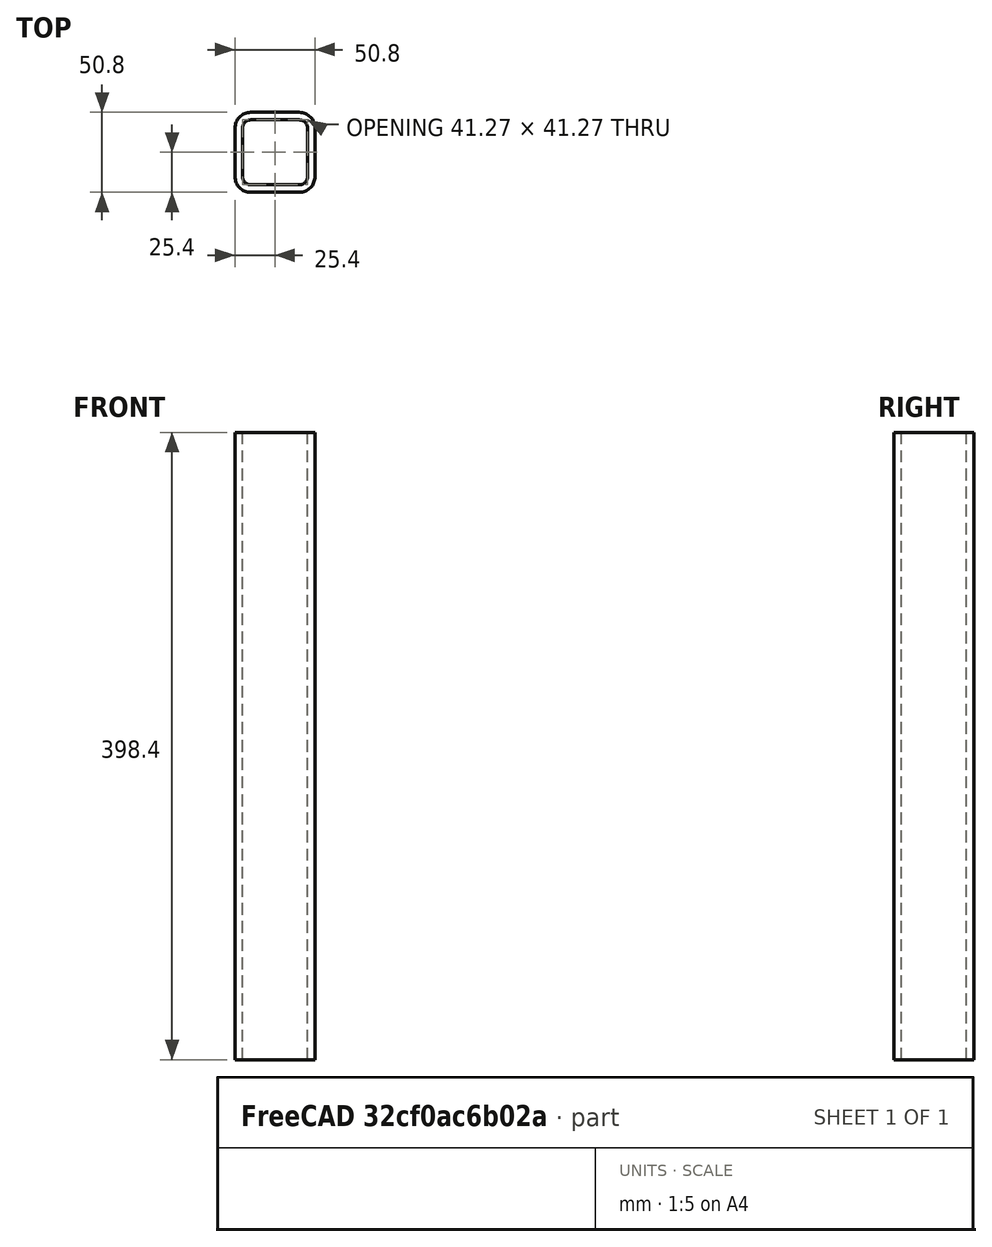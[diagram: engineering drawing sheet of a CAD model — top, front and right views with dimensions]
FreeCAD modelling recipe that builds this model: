
FCSTD DOCUMENT  (FreeCAD 0.19R23578 (Git))
Label: frame_side_piece
License: All rights reserved
LicenseURL: http://en.wikipedia.org/wiki/All_rights_reserved
objects: PartDesign::CoordinateSystem×2, Sketcher::SketchObject×1, PartDesign::Pad×1, PartDesign::Body×1, App::Part×1
note: 6 computed .brp shape members not serialized (recipe doc carries the construction recipe); baked Part::Feature solids carry a one-line shape summary decoded from their .brp

FEATURE [Sketcher::SketchObject] Sketch004
  MapMode = 5
  sketch-geometry (16):
    g0: LineSegment StartX=10 StartY=0 StartZ=0 EndX=40.8 EndY=0 EndZ=0
    g1: LineSegment StartX=50.8 StartY=10 StartZ=0 EndX=50.8 EndY=40.8 EndZ=0
    g2: LineSegment StartX=40.8 StartY=50.8 StartZ=0 EndX=10 EndY=50.8 EndZ=0
    g3: LineSegment StartX=0 StartY=40.8 StartZ=0 EndX=0 EndY=10 EndZ=0
    g4: ArcOfCircle CenterX=10 CenterY=40.8 CenterZ=0 NormalX=0 NormalY=0 NormalZ=1 AngleXU=0 Radius=10 StartAngle=1.5708 EndAngle=3.14159
    g5: ArcOfCircle CenterX=10 CenterY=10 CenterZ=0 NormalX=0 NormalY=0 NormalZ=1 AngleXU=0 Radius=10 StartAngle=3.14159 EndAngle=4.71239
    g6: ArcOfCircle CenterX=40.8 CenterY=10 CenterZ=0 NormalX=0 NormalY=0 NormalZ=1 AngleXU=0 Radius=10 StartAngle=4.71239 EndAngle=6.28319
    g7: ArcOfCircle CenterX=40.8 CenterY=40.8 CenterZ=0 NormalX=0 NormalY=0 NormalZ=1 AngleXU=0 Radius=10 StartAngle=0 EndAngle=1.5708
    g8: LineSegment StartX=10 StartY=46.0375 StartZ=0 EndX=40.8 EndY=46.0375 EndZ=0
    g9: LineSegment StartX=46.0375 StartY=40.8 StartZ=0 EndX=46.0375 EndY=10 EndZ=0
    g10: LineSegment StartX=40.8 StartY=4.7625 StartZ=0 EndX=10 EndY=4.7625 EndZ=0
    g11: LineSegment StartX=4.7625 StartY=10 StartZ=0 EndX=4.7625 EndY=40.8 EndZ=0
    g12: ArcOfCircle CenterX=10 CenterY=40.8 CenterZ=0 NormalX=0 NormalY=0 NormalZ=1 AngleXU=0 Radius=5.2375 StartAngle=1.5708 EndAngle=3.14159
    g13: ArcOfCircle CenterX=10 CenterY=10 CenterZ=0 NormalX=0 NormalY=0 NormalZ=1 AngleXU=0 Radius=5.2375 StartAngle=3.14159 EndAngle=4.71239
    g14: ArcOfCircle CenterX=40.8 CenterY=10 CenterZ=0 NormalX=0 NormalY=0 NormalZ=1 AngleXU=0 Radius=5.2375 StartAngle=4.71239 EndAngle=6.28319
    g15: ArcOfCircle CenterX=40.8 CenterY=40.8 CenterZ=0 NormalX=0 NormalY=0 NormalZ=1 AngleXU=0 Radius=5.2375 StartAngle=4e-16 EndAngle=1.5708
  constraints (36):
    c: Horizontal(g0)
    c: Horizontal(g2)
    c: Vertical(g1)
    c: Vertical(g3)
    c: Tangent(g2,g4) = -1.5708
    c: Tangent(g3,g4) = -1.5708
    c: Tangent(g3,g5) = -1.5708
    c: Tangent(g0,g5) = -1.5708
    c: Tangent(g0,g6) = -1.5708
    c: Tangent(g1,g6) = -1.5708
    c: Tangent(g2,g7) = -1.5708
    c: Tangent(g1,g7) = -1.5708
    c: Horizontal(g8)
    c: Horizontal(g10)
    c: Vertical(g9)
    c: Tangent(g8,g12) = 1.5708
    c: Tangent(g11,g12) = 1.5708
    c: Tangent(g11,g13) = 1.5708
    c: Tangent(g10,g13) = 1.5708
    c: Tangent(g9,g14) = 1.5708
    c: Tangent(g10,g14) = 1.5708
    c: Tangent(g8,g15) = 1.5708
    c: Tangent(g9,g15) = 1.5708
    c: PointOnObject(g3,g-2)
    c: PointOnObject(g0,g-1)
    c: DistanceX(g3,g1) = 50.8
    c: DistanceY(g0,g2) = 50.8
    c: Coincident(g13,g5)
    c: Coincident(g12,g4)
    c: Coincident(g7,g15)
    c: Coincident(g14,g6)
    c: Equal(g5,g4)
    c: Equal(g4,g7)
    c: Equal(g7,g6)
    c: DistanceX(g3,g0) = 10
    c: DistanceX(g9,g1) = 4.7625
FEATURE [PartDesign::Pad] Pad004
  AllowMultiFace = false
  Direction = (1,1,1)
  Length = 398.4
  Length2 = 100
  Profile = -> Sketch004
  Type = 0
FEATURE [PartDesign::Body] Body004
  Group = -> [Sketch004,Pad004]
  Tip = -> Pad004
FEATURE [PartDesign::CoordinateSystem] LCS_1
  AttacherType = Attacher::AttachEngine3D
  MapMode = 45
  Placement = pos=(25.4,25.4,398.4) rot=(0,0,1;0rad)
  Support = -> [Pad004]
FEATURE [PartDesign::CoordinateSystem] LCS_2
  AttacherType = Attacher::AttachEngine3D
  MapMode = 45
  Placement = pos=(25.4,25.4,0) rot=(0,0,1;0rad)
  Support = -> [Pad004]
FEATURE [App::Part] Part006  label="frame_side_piece"
  Group = -> [Body004,LCS_1,LCS_2]
  Origin = -> Origin007
